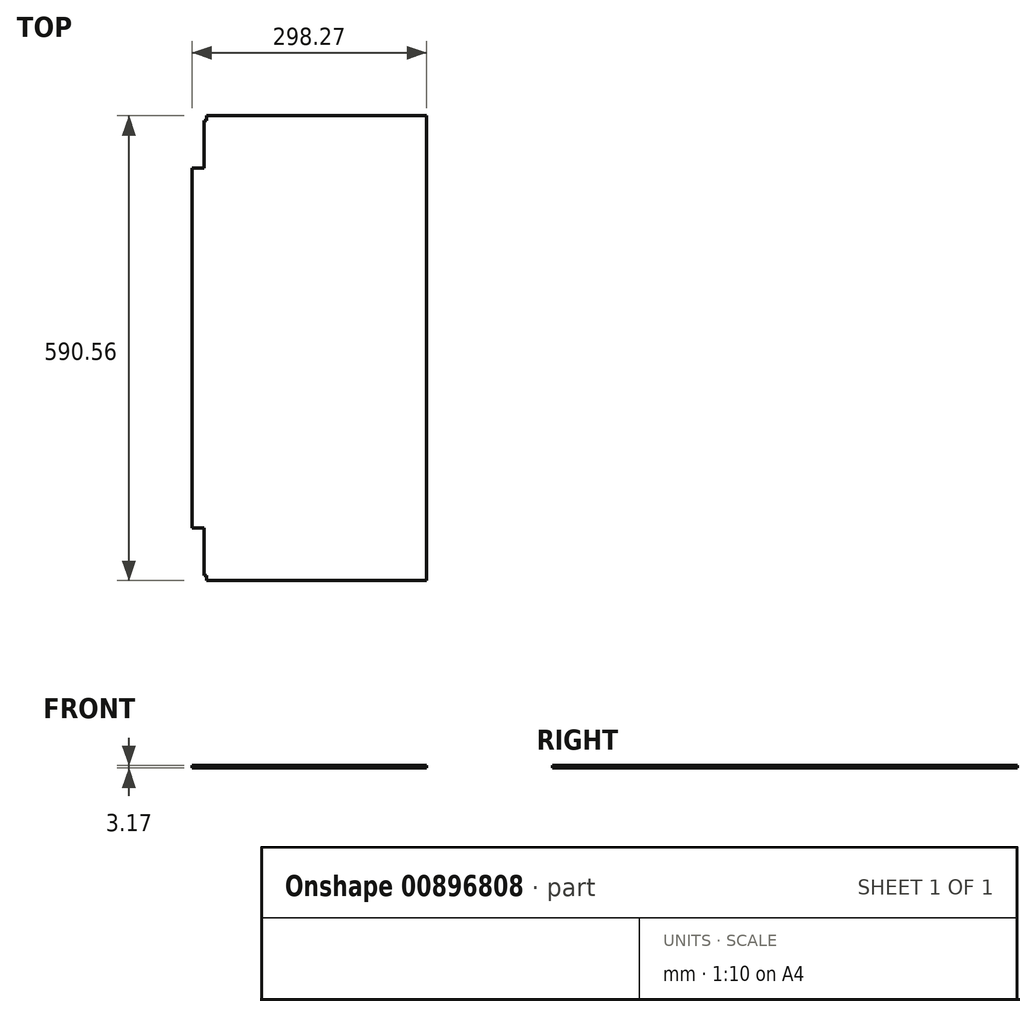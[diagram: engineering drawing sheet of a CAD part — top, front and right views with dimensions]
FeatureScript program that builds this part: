
annotation { "Feature Type Name" : "Feature", "Feature Type Description" : "" }
export const myFeature = defineFeature(function(context is Context, id is Id, definition is map)
    precondition{}
    {
        {
            var Q0;
            Q0=qCreatedBy(makeId("Top.planeOp"),FACE);
            var sketch = newSketch(context, id + "F0", { "sketchPlane" : qUnion([Q0])});
            skLineSegment(sketch, "E0.bottom", {"start": v(152.4, -295.28) * mm, "end": v(-127, -295.28) * mm});
            skLineSegment(sketch, "E0.top", {"start": v(152.4, 295.28) * mm, "end": v(-127, 295.28) * mm});
            skLineSegment(sketch, "E0.left", {"start": v(152.4, -295.27) * mm, "end": v(152.4, 295.28) * mm});
            skPoint(sketch, "E0.middle", {"position": v(0, 0) * mm});
            skLineSegment(sketch, "E1.bottom", {"start": v(-130.38, 288.93) * mm, "end": v(-127, 288.93) * mm});
            skLineSegment(sketch, "E1.top", {"start": v(-130.38, -288.93) * mm, "end": v(-127, -288.93) * mm});
            skLineSegment(sketch, "E2", {"start": v(-127, 288.93) * mm, "end": v(-127, 295.28) * mm});
            skPoint(sketch, "E3.orphan", {"position": v(-152.4, 295.27) * mm});
            skLineSegment(sketch, "E4", {"start": v(-127, -288.93) * mm, "end": v(-127, -295.28) * mm});
            skPoint(sketch, "E5.orphan", {"position": v(-152.4, -295.28) * mm});
            skLineSegment(sketch, "E6.right", {"start": v(-145.87, 228.6) * mm, "end": v(-145.87, -228.6) * mm});
            skPoint(sketch, "E6.middle", {"position": v(-152.4, 0) * mm});
            skPoint(sketch, "E0.right.start.orphan", {"position": v(-152.4, -288.93) * mm});
            skPoint(sketch, "E7.trimOffspring.end.orphan", {"position": v(-152.4, 288.93) * mm});
            skLineSegment(sketch, "E8", {"start": v(-130.38, 288.92) * mm, "end": v(-130.38, 228.6) * mm});
            skLineSegment(sketch, "E9", {"start": v(-130.38, -288.93) * mm, "end": v(-130.38, -228.6) * mm});
            skPoint(sketch, "E6.top.start.orphan", {"position": v(-158.93, -228.6) * mm});
            skLineSegment(sketch, "E10", {"start": v(-145.87, -228.6) * mm, "end": v(-130.38, -228.6) * mm});
            skLineSegment(sketch, "E11", {"start": v(0, 0) * mm, "end": v(-246.76, 0) * mm, "construction": true});
            skLineSegment(sketch, "E12", {"start": v(-145.87, 228.6) * mm, "end": v(-130.38, 228.6) * mm});
            skSolve(sketch);
        }
        {
            var Q0;
            Q0 = qSketchRegion(id + "F0", true);
            extrude(context, id + "F1", {"entities" : qUnion([Q0]), "depth" : 3.17 * mm, "offsetDistance" : 25.4 * mm});
        }
    });
